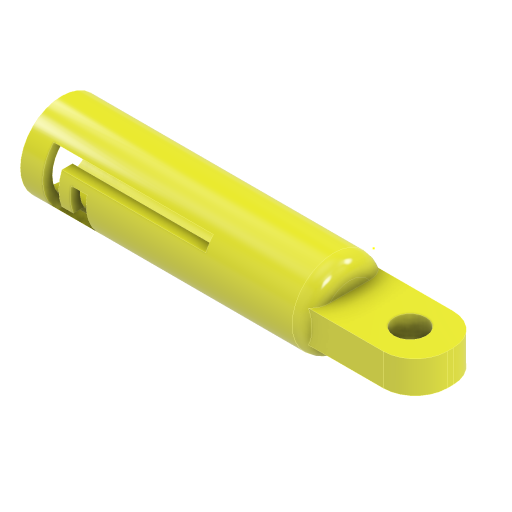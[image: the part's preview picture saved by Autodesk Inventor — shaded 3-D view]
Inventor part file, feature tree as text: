
AUTODESK INVENTOR PART (.ipt)
format: ipt  version: 2024 (Build 280153000, 153)  size: 241,664 bytes
history: native  units: mm
features: sketch x6, extrude x4, fillet x3, other x2, loft x1, shell x1
ambient origin geometry x8: Origin, YZ Plane, XZ Plane, XY Plane, X Axis, Y Axis, Z Axis, Center Point
bodies: Solido1 (feature_tree)
feature tree (17):
  sketch  "Schizzo1"
  sketch  "Schizzo2"
  other  "Piano di lavoro1"
  loft  "Loft1"
  shell  "Svuotamento1"  Thickness=90.0mm
  other  "Piano di lavoro3"
  sketch  "Schizzo11"
  extrude  "Estrusione5"  Depth=15.0mm
  extrude  "Estrusione6"  Depth=26.0mm
  fillet  "Raccordo1"  Radius=26.0mm
  fillet  "Raccordo2"  Radius=25.0mm
  extrude  "Estrusione7"  Depth=17.0mm
  fillet  "Raccordo3"  Radius=10.0mm
  extrude  "Estrusione8"  Depth=5.0mm
  sketch  "Schizzo3"
  sketch  "Schizzo12"
  sketch  "Schizzo13"
